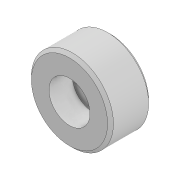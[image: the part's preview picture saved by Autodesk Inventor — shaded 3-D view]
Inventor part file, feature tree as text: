
AUTODESK INVENTOR PART (.ipt)
format: ipt  version: 2020.3 (Build 243373010, 373A)  size: 104,960 bytes
history: native  units: mm
features: sketch x2, extrude x2, hole x1, chamfer x1
ambient origin geometry x8: Origin, YZ Plane, XZ Plane, XY Plane, X Axis, Y Axis, Z Axis, Center Point
bodies: Solid1 (feature_tree)
feature tree (6):
  sketch  "Sketch1"  dims[d0=7.0mm d1=3.5mm d2=0.0mm]
  extrude  "Extrusion1"  Depth=3.5mm TaperAngle=0.0deg
  hole  "Hole1"  [1 undecoded]
  chamfer  "Chamfer1"  Distance=3.5mm
  extrude  "Extrusion2"  Depth=2.0mm TaperAngle=0.0deg
  sketch  "Sketch2"  dims[d3=1.729367mm d4=4.0mm d5=4.0mm d6=2.0mm d7=90.0deg d8=10.0mm d9=20.594885mm d10=0.25mm d11=2.0mm d12=45.0deg d13=3.5mm d14=2.0mm d15=0.0mm]
note: 1 required parameter value undecoded (feature->parameter linkage not recoverable at this tier; creation-order binding heuristic only, values carry confidence <= 0.55)
